# Revit family: Окно одностворчатое VEKA с фрамугой снизу
name_source: partatom
category: Окна
revit_build: Autodesk Revit 2016 (Build: 20150714_1515(x64)
units: mm (PartAtom-declared; Revit-internal decimal feet)

## family parameters
Всегда вертикально = Да
Заголовок OmniClass = Fixed Windows
Номер OmniClass = 23.30.20.17.11
Общий = Нет
Основа = Стена
При загрузке вырезать с полостями = Нет
Точка расчета площади = Нет

## types (5) — shared parameters
Rед = 1.0000 (м²·K)/Вт
VEKA_Завод-изготовитель = VEKA
VEKA_Лямбда краевой зоны стеклопакета = 0.0600 (м²·K)/Вт
Аналитическая конструкция = <Нет>
Замыкание стены = По основе
Наименование = ОП ОСП 15-9 Л
Обозначение = ГОСТ 23166-99
Описание = Окно
Отлив = VEKA_Окна_ПВХ<БелыйМатовый
Подоконник = VEKA_Окна_ПВХ<БелыйМатовый
Рама = VEKA_Окна_ПВХ<БелыйМатовый
Рама.Ширина = 80 мм
Стекло = Стекло
zero-valued in all types: Высота, Ширина

## per-type parameters (varying)
| type | VEKA_Rпрофиля | VEKA_Ширина профиля | Рама.Толщина |
| SOFTLINE 70 | 0.7800 (м²·K)/Вт | 118 мм | 70 мм |
| WHS 72 | 0.7700 (м²·K)/Вт | 111 мм | 72 мм |
| WHS 60 | 0.6600 (м²·K)/Вт | 106 мм | 60 мм |
| SOFTLINE 82 | 1.0600 (м²·K)/Вт | 124 мм | 82 мм |
| EUROLINE 58 | 0.6400 (м²·K)/Вт | 116 мм | 58 мм |

## geometry (parser evidence)
native form markers: Blend x4, Sweep x2
no freeform markers — native parametric forms only
